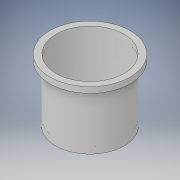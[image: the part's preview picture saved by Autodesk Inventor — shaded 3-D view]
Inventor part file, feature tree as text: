
AUTODESK INVENTOR PART (.ipt)
format: ipt  version: 2017 (Build 210142000, 142)  size: 143,872 bytes
history: native  units: in
note: dims shown in document units (in); Inventor stores cm internally (conversion verified against a paired STEP export)
features: revolve x1, sketch x1
ambient origin geometry x8: Origin, YZ Plane, XZ Plane, XY Plane, X Axis, Y Axis, Z Axis, Center Point
bodies: Body1 (feature_tree)
feature tree (2):
  revolve  "Revolution3"  [1 undecoded]
  sketch  "Sketch1"  dims[d0=1.13in d1=3.4in d2=0.25in d3=0.1718in d5=1.0in d6=1.0in d7=90.0deg d8=0.5in d9=15.0deg d11=0.25in d12=1.25in d13=0.25in d15=0.25in d16=0.5in d17=0.5in d18=0.5in d19=2.5in d20=0.5in d22=0.375in d23=0.25in d25=0.234in d26=15.0deg d29=90.0deg d30=2.65in]
note: 1 required parameter value undecoded (feature->parameter linkage not recoverable at this tier; creation-order binding heuristic only, values carry confidence <= 0.55)
